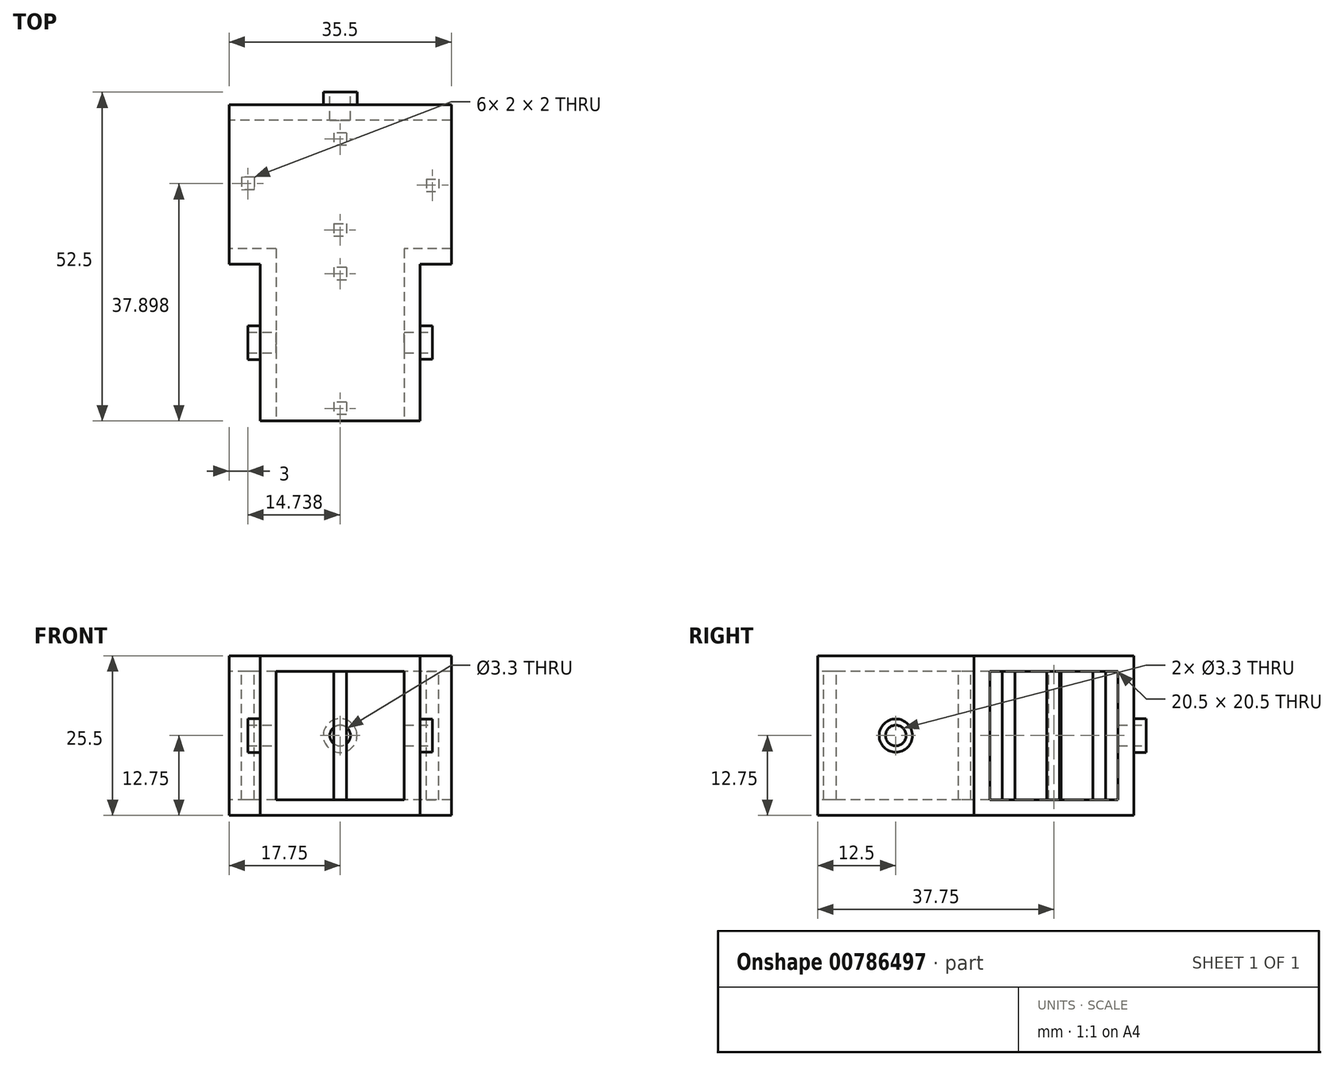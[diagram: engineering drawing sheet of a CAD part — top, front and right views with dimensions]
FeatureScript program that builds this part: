
annotation { "Feature Type Name" : "Feature", "Feature Type Description" : "" }
export const myFeature = defineFeature(function(context is Context, id is Id, definition is map)
    precondition{}
    {
        {
            var Q0;
            Q0=qCreatedBy(makeId("Front.planeOp"),FACE);
            var sketch = newSketch(context, id + "F0", { "sketchPlane" : qUnion([Q0])});
            skLineSegment(sketch, "E0.bottom", {"start": v(-17.75, 12.75) * mm, "end": v(17.75, 12.75) * mm});
            skLineSegment(sketch, "E0.top", {"start": v(-17.75, -12.75) * mm, "end": v(17.75, -12.75) * mm});
            skLineSegment(sketch, "E0.left", {"start": v(-17.75, 15.55) * mm, "end": v(-17.75, -12.75) * mm});
            skLineSegment(sketch, "E0.right", {"start": v(17.75, 12.75) * mm, "end": v(17.75, -12.75) * mm});
            skPoint(sketch, "E1", {"position": v(0, 0) * mm});
            skPoint(sketch, "E1.positionSnap0", {"position": v(17.75, 0) * mm});
            skPoint(sketch, "E1.positionSnap1", {"position": v(0, 12.75) * mm});
            skSolve(sketch);
        }
        {
            var Q0;
            Q0 = qSketchRegion(id + "F0", true);
            extrude(context, id + "F1", {"entities" : qUnion([Q0]), "depth" : 25.5 * mm, "offsetDistance" : 25 * mm});
        }
        {
            var Q0;
            Q0=makeQuery(id+"F1.opExtrude","SWEPT_FACE",FACE,{"disambiguationData":[OSD([sQuery(id+"F0.wireOp",EDGE,"E0.left")])]});
            var sketch = newSketch(context, id + "F2", { "sketchPlane" : qUnion([Q0])});
            skLineSegment(sketch, "E2.bottom", {"start": v(2.5, 10.25) * mm, "end": v(23, 10.25) * mm});
            skLineSegment(sketch, "E2.top", {"start": v(2.5, -10.25) * mm, "end": v(23, -10.25) * mm});
            skLineSegment(sketch, "E2.left", {"start": v(2.5, 10.25) * mm, "end": v(2.5, -10.25) * mm});
            skLineSegment(sketch, "E2.right", {"start": v(23, 10.25) * mm, "end": v(23, -10.25) * mm});
            skSolve(sketch);
        }
        {
            var Q0;
            Q0 = qSketchRegion(id + "F2", true);
            extrude(context, id + "F3", {"entities" : qUnion([Q0]), "operationType" : NewBodyOperationType.REMOVE, "oppositeDirection" : true, "depth" : 35.5 * mm, "offsetDistance" : 25 * mm});
        }
        {
            var Q0;
            Q0=makeQuery(id+"F1.opExtrude","CAP_FACE",FACE,{"disambiguationData":[OSD([sQuery(id+"F0.wireOp",EDGE,"E0.bottom"),sQuery(id+"F0.wireOp",EDGE,"E0.top"),sQuery(id+"F0.wireOp",EDGE,"E0.left"),sQuery(id+"F0.wireOp",EDGE,"E0.right")])],"isStart":false});
            var sketch = newSketch(context, id + "F4", { "sketchPlane" : qUnion([Q0])});
            skLineSegment(sketch, "E3.bottom", {"start": v(-12.75, 12.75) * mm, "end": v(12.75, 12.75) * mm});
            skLineSegment(sketch, "E3.top", {"start": v(-12.75, -12.75) * mm, "end": v(12.75, -12.75) * mm});
            skLineSegment(sketch, "E3.left", {"start": v(-12.75, 12.75) * mm, "end": v(-12.75, -12.75) * mm});
            skLineSegment(sketch, "E3.right", {"start": v(12.75, 12.75) * mm, "end": v(12.75, -12.75) * mm});
            skSolve(sketch);
        }
        {
            var Q0;
            Q0 = qSketchRegion(id + "F4", true);
            extrude(context, id + "F5", {"entities" : qUnion([Q0]), "operationType" : NewBodyOperationType.ADD, "depth" : 25 * mm, "offsetDistance" : 25 * mm});
        }
        {
            var Q0;
            Q0=makeQuery(id+"F5.opExtrude","CAP_FACE",FACE,{"disambiguationData":[OSD([sQuery(id+"F4.wireOp",EDGE,"E3.bottom"),sQuery(id+"F4.wireOp",EDGE,"E3.top"),sQuery(id+"F4.wireOp",EDGE,"E3.left"),sQuery(id+"F4.wireOp",EDGE,"E3.right")])],"isStart":false});
            var sketch = newSketch(context, id + "F6", { "sketchPlane" : qUnion([Q0])});
            skLineSegment(sketch, "E4.bottom", {"start": v(-10.25, 10.25) * mm, "end": v(10.25, 10.25) * mm});
            skLineSegment(sketch, "E4.top", {"start": v(-10.25, -10.25) * mm, "end": v(10.25, -10.25) * mm});
            skLineSegment(sketch, "E4.left", {"start": v(-10.25, 10.25) * mm, "end": v(-10.25, -10.25) * mm});
            skLineSegment(sketch, "E4.right", {"start": v(10.25, 10.25) * mm, "end": v(10.25, -10.25) * mm});
            skSolve(sketch);
        }
        {
            var Q0;
            Q0 = qSketchRegion(id + "F6", true);
            extrude(context, id + "F7", {"entities" : qUnion([Q0]), "operationType" : NewBodyOperationType.REMOVE, "oppositeDirection" : true, "depth" : 38 * mm, "offsetDistance" : 25 * mm});
        }
        {
            var Q0;
            Q0=makeQuery(id+"F5.opExtrude","SWEPT_FACE",FACE,{"disambiguationData":[OSD([sQuery(id+"F4.wireOp",EDGE,"E3.right")])]});
            var sketch = newSketch(context, id + "F8", { "sketchPlane" : qUnion([Q0])});
            skCircle(sketch, "E5", {"center": v(-38, 0) * mm, "radius": 2.65 * mm});
            skPoint(sketch, "E5.centerSnap0", {"position": v(-38, -12.75) * mm});
            skPoint(sketch, "E5.centerSnap1", {"position": v(-50.5, 0) * mm});
            skSolve(sketch);
        }
        {
            var Q0;
            Q0 = qSketchRegion(id + "F8", true);
            extrude(context, id + "F9", {"entities" : qUnion([Q0]), "operationType" : NewBodyOperationType.ADD, "depth" : 2 * mm, "offsetDistance" : 25 * mm});
        }
        {
            var Q0;
            Q0=makeQuery(id+"F9.opExtrude","CAP_FACE",FACE,{"disambiguationData":[OSD([sQuery(id+"F8.wireOp",EDGE,"E5")])],"isStart":false});
            var sketch = newSketch(context, id + "F10", { "sketchPlane" : qUnion([Q0])});
            skCircle(sketch, "E6", {"center": v(-38, 0) * mm, "radius": 1.65 * mm});
            skSolve(sketch);
        }
        {
            var Q0;
            Q0 = qSketchRegion(id + "F10", true);
            extrude(context, id + "F11", {"entities" : qUnion([Q0]), "operationType" : NewBodyOperationType.REMOVE, "endBound" : BoundingType.THROUGH_ALL, "oppositeDirection" : true, "depth" : 30 * mm, "offsetDistance" : 25 * mm});
        }
        {
            var Q0;
            Q0=makeQuery(id+"F5.opExtrude","SWEPT_FACE",FACE,{"disambiguationData":[OSD([sQuery(id+"F4.wireOp",EDGE,"E3.left")])]});
            var sketch = newSketch(context, id + "F12", { "sketchPlane" : qUnion([Q0])});
            skCircle(sketch, "E7", {"center": v(38, 0) * mm, "radius": 2.7 * mm});
            skSolve(sketch);
        }
        {
            var Q0;
            Q0 = qSketchRegion(id + "F12", true);
            extrude(context, id + "F13", {"entities" : qUnion([Q0]), "operationType" : NewBodyOperationType.ADD, "depth" : 2 * mm, "offsetDistance" : 25 * mm});
        }
        {
            var Q0;
            Q0=makeQuery(id+"F13.opExtrude","CAP_FACE",FACE,{"disambiguationData":[OSD([sQuery(id+"F12.wireOp",EDGE,"E7")])],"isStart":false});
            var sketch = newSketch(context, id + "F14", { "sketchPlane" : qUnion([Q0])});
            skCircle(sketch, "E8", {"center": v(38, 0) * mm, "radius": 1.65 * mm});
            skSolve(sketch);
        }
        {
            var Q0;
            Q0 = qSketchRegion(id + "F14", true);
            extrude(context, id + "F15", {"entities" : qUnion([Q0]), "operationType" : NewBodyOperationType.REMOVE, "oppositeDirection" : true, "depth" : 5.5 * mm, "offsetDistance" : 25 * mm});
        }
        {
            var Q0;
            Q0=makeQuery(id+"F1.opExtrude","CAP_FACE",FACE,{"disambiguationData":[OSD([sQuery(id+"F0.wireOp",EDGE,"E0.bottom"),sQuery(id+"F0.wireOp",EDGE,"E0.top"),sQuery(id+"F0.wireOp",EDGE,"E0.left"),sQuery(id+"F0.wireOp",EDGE,"E0.right")])],"isStart":true});
            var sketch = newSketch(context, id + "F16", { "sketchPlane" : qUnion([Q0])});
            skCircle(sketch, "E9", {"center": v(0, 0) * mm, "radius": 2.7 * mm});
            skSolve(sketch);
        }
        {
            var Q0;
            Q0 = qSketchRegion(id + "F16", true);
            extrude(context, id + "F17", {"entities" : qUnion([Q0]), "operationType" : NewBodyOperationType.ADD, "depth" : 2 * mm, "offsetDistance" : 25 * mm});
        }
        {
            var Q0;
            Q0=makeQuery(id+"F17.opExtrude","CAP_FACE",FACE,{"disambiguationData":[OSD([sQuery(id+"F16.wireOp",EDGE,"E9")])],"isStart":false});
            var sketch = newSketch(context, id + "F18", { "sketchPlane" : qUnion([Q0])});
            skCircle(sketch, "E10", {"center": v(0, 0) * mm, "radius": 1.65 * mm});
            skSolve(sketch);
        }
        {
            var Q0;
            Q0 = qSketchRegion(id + "F18", true);
            extrude(context, id + "F19", {"entities" : qUnion([Q0]), "operationType" : NewBodyOperationType.REMOVE, "oppositeDirection" : true, "depth" : 5.5 * mm, "offsetDistance" : 25 * mm});
        }
        {
            var Q0;
            Q0=makeQuery(id+"F7.boolean.opBoolean","MERGE",FACE,{"derivedFrom":[makeQuery(id+"F3.boolean.opBoolean","COPY",FACE,{"derivedFrom":makeQuery(id+"F3.opExtrude","SWEPT_FACE",FACE,{"disambiguationData":[OSD([sQuery(id+"F2.wireOp",EDGE,"E2.bottom")])]})}),makeQuery(id+"F7.opExtrude","SWEPT_FACE",FACE,{"disambiguationData":[OSD([sQuery(id+"F6.wireOp",EDGE,"E4.bottom")])]})]});
            var sketch = newSketch(context, id + "F20", { "sketchPlane" : qUnion([Q0])});
            skLineSegment(sketch, "E11.bottom", {"start": v(1, 26) * mm, "end": v(-1, 26) * mm});
            skLineSegment(sketch, "E11.top", {"start": v(1, 28) * mm, "end": v(-1, 28) * mm});
            skLineSegment(sketch, "E11.left", {"start": v(1, 26) * mm, "end": v(1, 28) * mm});
            skLineSegment(sketch, "E11.right", {"start": v(-1, 26) * mm, "end": v(-1, 28) * mm});
            skLineSegment(sketch, "E12.bottom", {"start": v(1, 47.5) * mm, "end": v(-1, 47.5) * mm});
            skLineSegment(sketch, "E12.top", {"start": v(1, 49.5) * mm, "end": v(-1, 49.5) * mm});
            skLineSegment(sketch, "E12.left", {"start": v(1, 47.5) * mm, "end": v(1, 49.5) * mm});
            skLineSegment(sketch, "E12.right", {"start": v(-1, 47.5) * mm, "end": v(-1, 49.5) * mm});
            skSolve(sketch);
        }
        {
            var Q0;
            Q0 = qSketchRegion(id + "F20", true);
            extrude(context, id + "F21", {"entities" : qUnion([Q0]), "operationType" : NewBodyOperationType.ADD, "depth" : 20.5 * mm, "offsetDistance" : 25 * mm});
        }
        {
            var Q0;
            Q0=makeQuery(id+"F7.boolean.opBoolean","MERGE",FACE,{"derivedFrom":[makeQuery(id+"F3.boolean.opBoolean","COPY",FACE,{"derivedFrom":makeQuery(id+"F3.opExtrude","SWEPT_FACE",FACE,{"disambiguationData":[OSD([sQuery(id+"F2.wireOp",EDGE,"E2.bottom")])]})}),makeQuery(id+"F7.opExtrude","SWEPT_FACE",FACE,{"disambiguationData":[OSD([sQuery(id+"F6.wireOp",EDGE,"E4.bottom")])]})]});
            var sketch = newSketch(context, id + "F22", { "sketchPlane" : qUnion([Q0])});
            skLineSegment(sketch, "E13.bottom", {"start": v(1, 4.5) * mm, "end": v(-1, 4.5) * mm});
            skLineSegment(sketch, "E13.top", {"start": v(1, 6.5) * mm, "end": v(-1, 6.5) * mm});
            skLineSegment(sketch, "E13.left", {"start": v(1, 4.5) * mm, "end": v(1, 6.5) * mm});
            skLineSegment(sketch, "E13.right", {"start": v(-1, 4.5) * mm, "end": v(-1, 6.5) * mm});
            skLineSegment(sketch, "E14.bottom", {"start": v(-13.75, 11.6) * mm, "end": v(-15.75, 11.6) * mm});
            skLineSegment(sketch, "E14.top", {"start": v(-13.75, 13.6) * mm, "end": v(-15.75, 13.6) * mm});
            skLineSegment(sketch, "E14.left", {"start": v(-13.75, 11.6) * mm, "end": v(-13.75, 13.6) * mm});
            skLineSegment(sketch, "E14.right", {"start": v(-15.75, 11.6) * mm, "end": v(-15.75, 13.6) * mm});
            skLineSegment(sketch, "E15.bottom", {"start": v(13.75, 11.87) * mm, "end": v(15.75, 11.87) * mm});
            skLineSegment(sketch, "E15.top", {"start": v(13.75, 13.87) * mm, "end": v(15.75, 13.87) * mm});
            skLineSegment(sketch, "E15.left", {"start": v(13.75, 11.87) * mm, "end": v(13.75, 13.87) * mm});
            skLineSegment(sketch, "E15.right", {"start": v(15.75, 11.87) * mm, "end": v(15.75, 13.87) * mm});
            skLineSegment(sketch, "E16.bottom", {"start": v(-1.01, 19) * mm, "end": v(0.99, 19) * mm});
            skLineSegment(sketch, "E16.top", {"start": v(-1.01, 21) * mm, "end": v(0.99, 21) * mm});
            skLineSegment(sketch, "E16.left", {"start": v(-1.01, 19) * mm, "end": v(-1.01, 21) * mm});
            skLineSegment(sketch, "E16.right", {"start": v(0.99, 19) * mm, "end": v(0.99, 21) * mm});
            skSolve(sketch);
        }
        {
            var Q0;
            Q0 = qSketchRegion(id + "F22", true);
            extrude(context, id + "F23", {"entities" : qUnion([Q0]), "operationType" : NewBodyOperationType.ADD, "depth" : 20.5 * mm, "offsetDistance" : 25 * mm});
        }
    });
